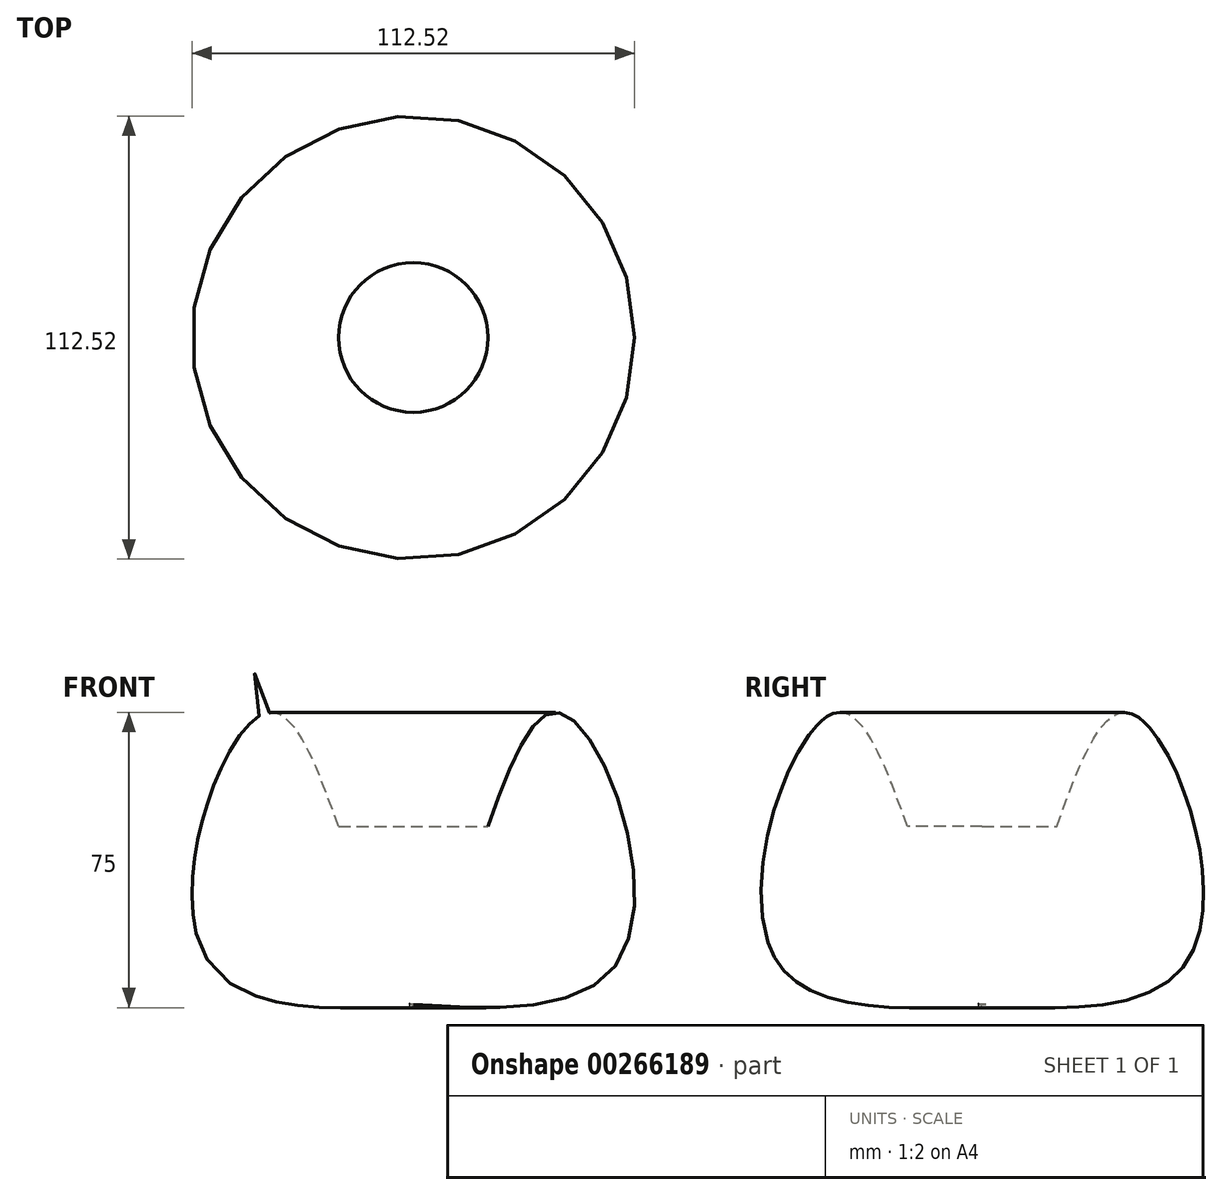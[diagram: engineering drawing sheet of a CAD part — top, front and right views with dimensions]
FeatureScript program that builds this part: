
annotation { "Feature Type Name" : "Feature", "Feature Type Description" : "" }
export const myFeature = defineFeature(function(context is Context, id is Id, definition is map)
    precondition{}
    {
        {
            var Q0;
            Q0=qCreatedBy(makeId("Front.planeOp"),FACE);
            var sketch = newSketch(context, id + "F0", { "sketchPlane" : qUnion([Q0])});
            skLineSegment(sketch, "E0", {"start": v(0, 0) * mm, "end": v(0, 32.82) * mm});
            skLineSegment(sketch, "E1", {"start": v(0, 32.82) * mm, "end": v(18.99, 32.82) * mm});
            skFitSpline(sketch, "E2", {"points": [v(18.99, 32.82) * mm, v(38.53, 61.2) * mm, v(50.33, -3.87) * mm, v(0, -12.54) * mm, v(0, -12.9) * mm], "startDerivative": vector(64.31, 179.01) * mm, "endDerivative": vector(8.74, -15.2) * mm});
            skLineSegment(sketch, "E3", {"start": v(0, 0) * mm, "end": v(0, -12.54) * mm});
            skSolve(sketch);
        }
        {
            var Q0;
            Q0=makeQuery(id+"F0.imprint","IMPRINT",FACE,{"disambiguationData":[TD([[makeQuery(id+"F0.imprint","IMPRINT",EDGE,{"derivedFrom":sQuery(id+"F0.wireOp",EDGE,"E0")}),-1.0]])]});
            var Q1;
            Q1=sQuery(id+"F0.wireOp",EDGE,"E0");
            revolve(context, id + "F1", {"entities" : qUnion([Q0]), "axis" : qUnion([Q1]), "revolveType" : RevolveType.FULL});
        }
    });
